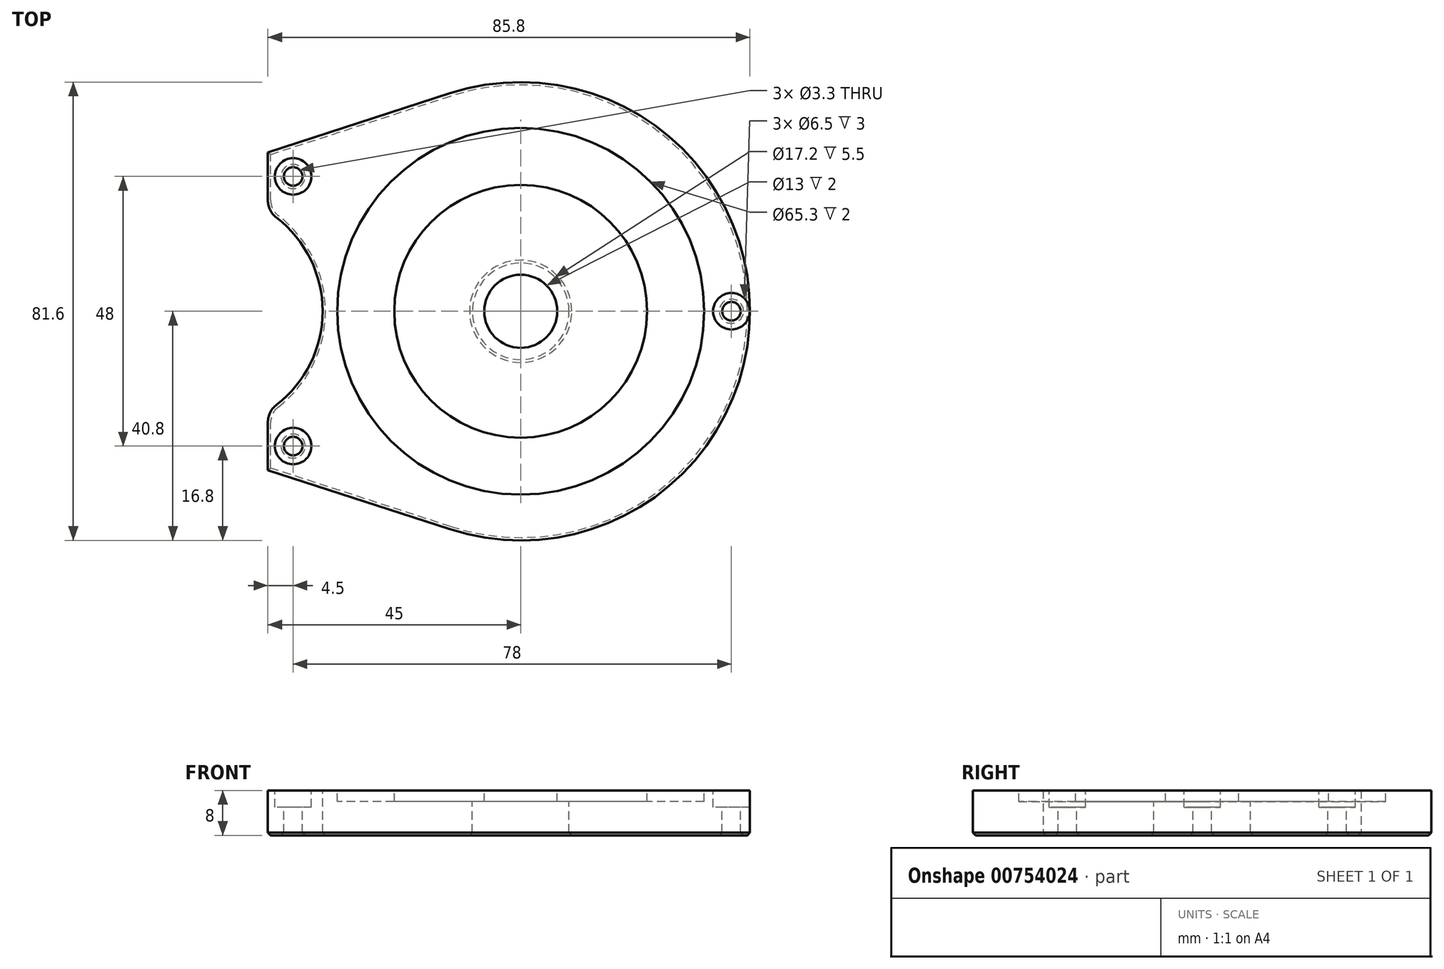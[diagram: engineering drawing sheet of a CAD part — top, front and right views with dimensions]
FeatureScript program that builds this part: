
annotation { "Feature Type Name" : "Feature", "Feature Type Description" : "" }
export const myFeature = defineFeature(function(context is Context, id is Id, definition is map)
    precondition{}
    {
        {
            var Q0;
            Q0=qCreatedBy(makeId("Top.planeOp"),FACE);
            var sketch = newSketch(context, id + "F0", { "sketchPlane" : qUnion([Q0])});
            skCircle(sketch, "E0", {"center": v(0, 0) * mm, "radius": 40.8 * mm});
            skSolve(sketch);
        }
        {
            var Q0;
            Q0=qSketchRegion(id+"F0",true);
            extrude(context, id + "F1", {"entities" : qUnion([Q0]), "depth" : 8 * mm});
        }
        {
            var Q0;
            Q0=qCreatedBy(makeId("Right.planeOp"),FACE);
            var sketch = newSketch(context, id + "F2", { "sketchPlane" : qUnion([Q0])});
            skLineSegment(sketch, "E1", {"start": v(0, 0) * mm, "end": v(0, 8) * mm});
            skLineSegment(sketch, "E2", {"start": v(0, 8) * mm, "end": v(6.5, 8) * mm});
            skLineSegment(sketch, "E3", {"start": v(6.5, 8) * mm, "end": v(6.5, 6) * mm});
            skLineSegment(sketch, "E4", {"start": v(6.5, 6) * mm, "end": v(8.6, 6) * mm});
            skLineSegment(sketch, "E5", {"start": v(8.6, 6) * mm, "end": v(8.6, 0) * mm});
            skLineSegment(sketch, "E6", {"start": v(8.6, 0) * mm, "end": v(0, 0) * mm});
            skLineSegment(sketch, "E7", {"start": v(0, 8) * mm, "end": v(0, 13.47) * mm, "construction": true});
            skSolve(sketch);
        }
        {
            var Q0;
            Q0=qSketchRegion(id+"F2",true);
            var Q1;
            Q1=sQuery(id+"F2.wireOp",EDGE,"E7");
            revolve(context, id + "F3", {"operationType" : NewBodyOperationType.REMOVE, "entities" : qUnion([Q0]), "axis" : qUnion([Q1]), "revolveType" : RevolveType.FULL, "oppositeDirection" : true});
        }
        {
            var Q0;
            Q0=makeQuery(id+"F1.opExtrude","CAP_FACE",FACE,{"disambiguationData":[OSD([sQuery(id+"F0.wireOp",EDGE,"E0")])],"isStart":false});
            var sketch = newSketch(context, id + "F4", { "sketchPlane" : qUnion([Q0])});
            skCircle(sketch, "E8", {"center": v(0, 0) * mm, "radius": 22.5 * mm});
            skCircle(sketch, "E9", {"center": v(0, 0) * mm, "radius": 32.65 * mm});
            skSolve(sketch);
        }
        {
            var Q0;
            Q0 = qSketchRegion(id + "F4", true);
            extrude(context, id + "F5", {"entities" : qUnion([Q0]), "operationType" : NewBodyOperationType.REMOVE, "oppositeDirection" : true, "depth" : 2 * mm, "offsetDistance" : 25 * mm});
        }
        {
            var Q0;
            Q0=qCreatedBy(makeId("Top.planeOp"),FACE);
            var sketch = newSketch(context, id + "F6", { "sketchPlane" : qUnion([Q0])});
            skLineSegment(sketch, "E10.bottom", {"start": v(-36, 19.2) * mm, "end": v(-40.8, 19.2) * mm});
            skLineSegment(sketch, "E10.top", {"start": v(-36, -19.2) * mm, "end": v(-40.8, -19.2) * mm});
            skLineSegment(sketch, "E10.left", {"start": v(-36, 19.2) * mm, "end": v(-36, -19.2) * mm});
            skLineSegment(sketch, "E10.right", {"start": v(-40.8, 19.2) * mm, "end": v(-40.8, -19.2) * mm});
            skSolve(sketch);
        }
        {
            var Q0;
            Q0=qSketchRegion(id+"F6",true);
            extrude(context, id + "F7", {"entities" : qUnion([Q0]), "operationType" : NewBodyOperationType.REMOVE, "endBound" : BoundingType.THROUGH_ALL, "depth" : 25 * mm});
        }
        {
            var Q0;
            Q0=qCreatedBy(makeId("Top.planeOp"),FACE);
            var sketch = newSketch(context, id + "F8", { "sketchPlane" : qUnion([Q0])});
            skLineSegment(sketch, "E11", {"start": v(-45, -28.28) * mm, "end": v(-45, 28.28) * mm});
            skLineSegment(sketch, "E12", {"start": v(-45, 28.28) * mm, "end": v(-12.6, 38.8) * mm});
            skLineSegment(sketch, "E13", {"start": v(0, 0) * mm, "end": v(-51.86, 0) * mm, "construction": true});
            skArc(sketch, "E14.0", {"start": v(-12.6, 38.8) * mm, "mid": v(-26.2, 31.27) * mm, "end": v(-36, 19.2) * mm});
            skPoint(sketch, "E15.orphan", {"position": v(-36, -19.2) * mm});
            skLineSegment(sketch, "E16.MirrorCS", {"start": v(-45, -28.28) * mm, "end": v(-12.6, -38.8) * mm});
            skArc(sketch, "E17.MirrorCS", {"start": v(-12.6, -38.8) * mm, "mid": v(-26.2, -31.27) * mm, "end": v(-36, -19.2) * mm});
            skLineSegment(sketch, "E18", {"start": v(-36, 19.2) * mm, "end": v(-36, -19.2) * mm});
            skSolve(sketch);
        }
        {
            var Q0;
            Q0=qSketchRegion(id+"F8",true);
            var Q1;
            {var subQ0=sQuery(id+"F0.wireOp",EDGE,"E0");Q1=makeQuery(id+"FxYBaZk4sUh2lm1_1.boolean.opBoolean","SPLIT",FACE,{"disambiguationData":[TD([makeQuery(id+"F1.opExtrude","SWEPT_FACE",FACE,{"disambiguationData":[OSD([subQ0])]})])],"derivedFrom":makeQuery(id+"F1.opExtrude","CAP_FACE",FACE,{"disambiguationData":[OSD([subQ0])],"isStart":false})});}
            extrude(context, id + "F9", {"entities" : qUnion([Q0]), "operationType" : NewBodyOperationType.ADD, "endBound" : BoundingType.UP_TO_SURFACE, "endBoundEntityFace" : qUnion([Q1]), "depth" : 25 * mm});
        }
        {
            var Q0;
            {var subQ0=sQuery(id+"F0.wireOp",EDGE,"E0");Q0=makeQuery(id+"F9.boolean.opBoolean","MERGE",FACE,{"derivedFrom":[makeQuery(id+"FxYBaZk4sUh2lm1_1.boolean.opBoolean","SPLIT",FACE,{"disambiguationData":[TD([makeQuery(id+"F1.opExtrude","SWEPT_FACE",FACE,{"disambiguationData":[OSD([subQ0])]})])],"derivedFrom":makeQuery(id+"F1.opExtrude","CAP_FACE",FACE,{"disambiguationData":[OSD([subQ0])],"isStart":false})}),makeQuery(id+"F9.opExtrude","CAP_FACE",FACE,{"disambiguationData":[OSD([sQuery(id+"F8.wireOp",EDGE,"E11"),sQuery(id+"F8.wireOp",EDGE,"E12"),sQuery(id+"F8.wireOp",EDGE,"E14.0"),sQuery(id+"F8.wireOp",EDGE,"E16.MirrorCS"),sQuery(id+"F8.wireOp",EDGE,"E17.MirrorCS"),sQuery(id+"F8.wireOp",EDGE,"E18")])],"isStart":false})]});}
            var sketch = newSketch(context, id + "F10", { "sketchPlane" : qUnion([Q0])});
            skCircle(sketch, "E19", {"center": v(-56.25, 0) * mm, "radius": 21 * mm});
            skLineSegment(sketch, "E20", {"start": v(-56.25, 0) * mm, "end": v(0, 0) * mm, "construction": true});
            skSolve(sketch);
        }
        {
            var Q0;
            Q0=qSketchRegion(id+"F10",true);
            extrude(context, id + "F11", {"entities" : qUnion([Q0]), "operationType" : NewBodyOperationType.REMOVE, "endBound" : BoundingType.THROUGH_ALL, "oppositeDirection" : true, "depth" : 25 * mm});
        }
        {
            var Q0;
            Q0=makeQuery(id+"F11.boolean.opBoolean","INTERSECT",EDGE,{"disambiguationData":[OD(1.0)],"derivedFrom":[makeQuery(id+"F9.opExtrude","SWEPT_FACE",FACE,{"disambiguationData":[OSD([sQuery(id+"F8.wireOp",EDGE,"E11")])]}),makeQuery(id+"F11.opExtrude","SWEPT_FACE",FACE,{"disambiguationData":[OSD([sQuery(id+"F10.wireOp",EDGE,"E19")])]})]});
            var Q1;
            Q1=makeQuery(id+"F11.boolean.opBoolean","INTERSECT",EDGE,{"disambiguationData":[OD(0.0)],"derivedFrom":[makeQuery(id+"F9.opExtrude","SWEPT_FACE",FACE,{"disambiguationData":[OSD([sQuery(id+"F8.wireOp",EDGE,"E11")])]}),makeQuery(id+"F11.opExtrude","SWEPT_FACE",FACE,{"disambiguationData":[OSD([sQuery(id+"F10.wireOp",EDGE,"E19")])]})]});
            fillet(context, id + "F12", {"entities" : qUnion([Q0, Q1]), "radius" : 4 * mm, "tangentPropagation" : true, "allowEdgeOverflow" : false});
        }
        {
            var Q0;
            {var subQ0=sQuery(id+"F0.wireOp",EDGE,"E0");Q0=makeQuery(id+"F9.boolean.opBoolean","MERGE",FACE,{"derivedFrom":[makeQuery(id+"FxYBaZk4sUh2lm1_1.boolean.opBoolean","SPLIT",FACE,{"disambiguationData":[TD([makeQuery(id+"F1.opExtrude","SWEPT_FACE",FACE,{"disambiguationData":[OSD([subQ0])]})])],"derivedFrom":makeQuery(id+"F1.opExtrude","CAP_FACE",FACE,{"disambiguationData":[OSD([subQ0])],"isStart":false})}),makeQuery(id+"F9.opExtrude","CAP_FACE",FACE,{"disambiguationData":[OSD([sQuery(id+"F8.wireOp",EDGE,"E11"),sQuery(id+"F8.wireOp",EDGE,"E12"),sQuery(id+"F8.wireOp",EDGE,"E14.0"),sQuery(id+"F8.wireOp",EDGE,"E16.MirrorCS"),sQuery(id+"F8.wireOp",EDGE,"E17.MirrorCS"),sQuery(id+"F8.wireOp",EDGE,"E18")])],"isStart":false})]});}
            var sketch = newSketch(context, id + "F13", { "sketchPlane" : qUnion([Q0])});
            skPoint(sketch, "E21", {"position": v(-40.5, 24) * mm});
            skPoint(sketch, "E22", {"position": v(37.5, 0) * mm});
            skLineSegment(sketch, "E23", {"start": v(0, 0) * mm, "end": v(47.97, 0) * mm, "construction": true});
            skPoint(sketch, "E24.MirrorP", {"position": v(-40.5, -24) * mm});
            skSolve(sketch);
        }
        {
            var Q0;
            Q0=sQuery(id+"F13.wireOp",VERTEX,"E21");
            var Q1;
            Q1=sQuery(id+"F13.wireOp",VERTEX,"E24.MirrorP");
            var Q2;
            Q2=sQuery(id+"F13.wireOp",VERTEX,"E22");
            var Q3;
            Q3=makeQuery(id+"F1.opExtrude","SWEPT_BODY",BODY,{"disambiguationData":[OSD([sQuery(id+"F0.wireOp",EDGE,"E0")])]});
            hole(context, id + "F14", {"style" : HoleStyle.C_BORE, "endStyle" : HoleEndStyle.THROUGH, "standardTappedOrClearance" : lookupTablePath({ "standard" : "ISO", "fit" : "Normal", "size" : "M3", "type" : "Clearance" }), "standardBlindInLast" : lookupTablePath({ "fit" : "Standard", "standard" : "ISO", "size" : "M3", "type" : "Clearance" }), "holeDiameter" : 3.3 * mm, "cBoreDiameter" : 6.5 * mm, "cBoreDepth" : 3 * mm, "tappedDepth" : 12 * mm, "tapClearance" : 3, "locations" : qUnion([Q0, Q1, Q2]), "scope" : qUnion([Q3])});
        }
        {
            var Q0;
            Q0=makeQuery(id+"F9.boolean.opBoolean","MERGE",FACE,{"derivedFrom":[makeQuery(id+"F1.opExtrude","CAP_FACE",FACE,{"disambiguationData":[OSD([sQuery(id+"F0.wireOp",EDGE,"E0")])],"isStart":true}),makeQuery(id+"F9.opExtrude","CAP_FACE",FACE,{"disambiguationData":[OSD([sQuery(id+"F8.wireOp",EDGE,"E11"),sQuery(id+"F8.wireOp",EDGE,"E12"),sQuery(id+"F8.wireOp",EDGE,"E14.0"),sQuery(id+"F8.wireOp",EDGE,"E16.MirrorCS"),sQuery(id+"F8.wireOp",EDGE,"E17.MirrorCS"),sQuery(id+"F8.wireOp",EDGE,"E18")])],"isStart":true})]});
            chamfer(context, id + "F15", {"entities" : qUnion([Q0]), "width" : .5 * mm, "tangentPropagation" : true});
        }
    });
